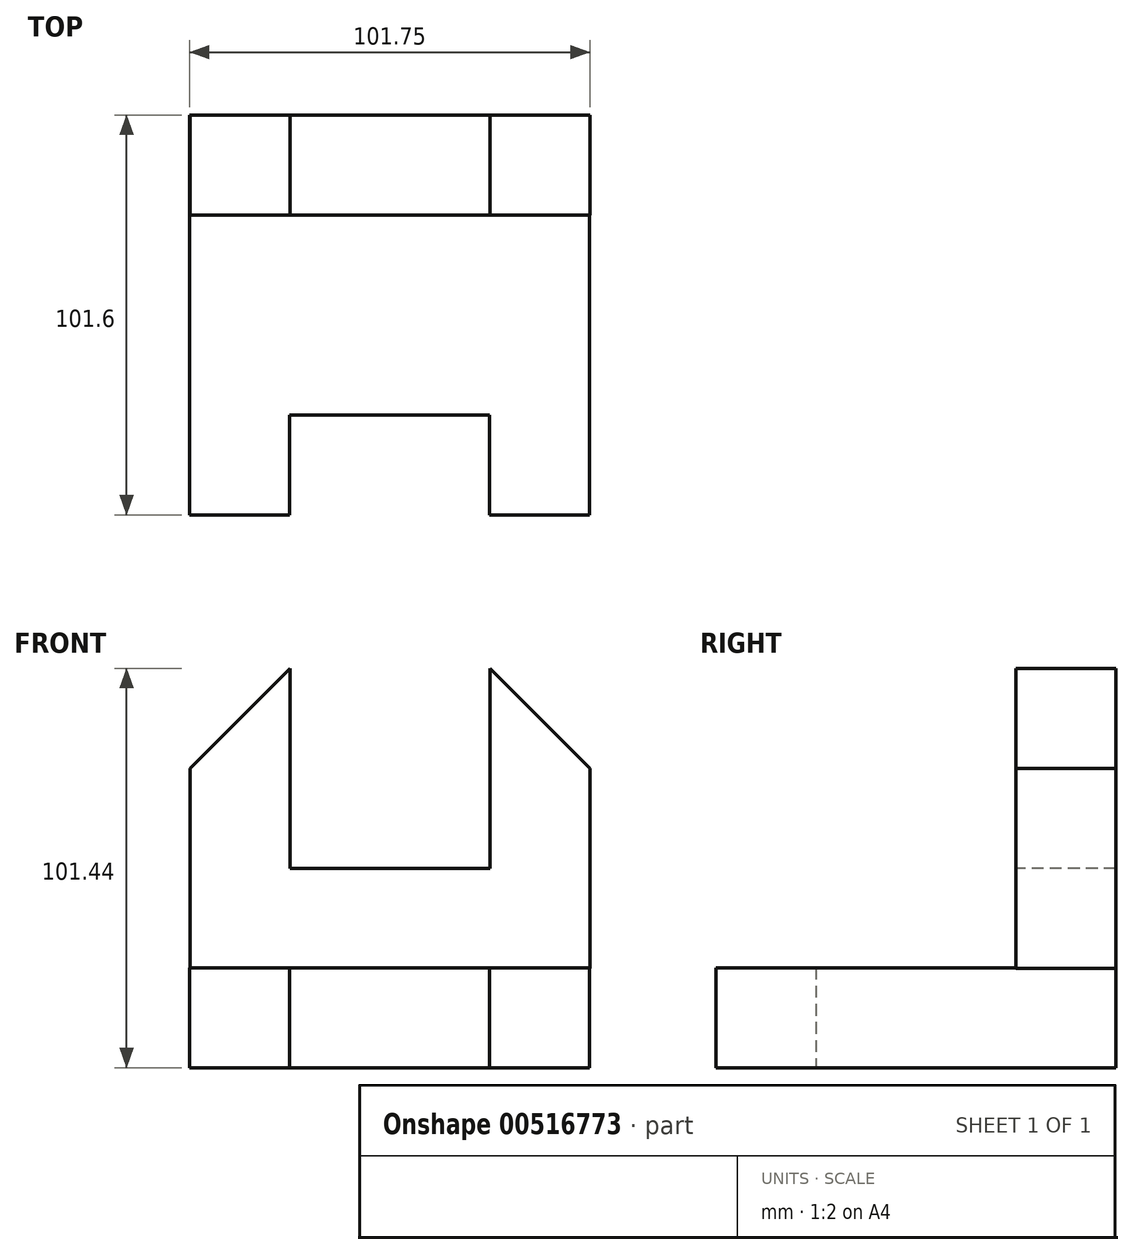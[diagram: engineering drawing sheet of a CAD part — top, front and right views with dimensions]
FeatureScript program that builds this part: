
annotation { "Feature Type Name" : "Feature", "Feature Type Description" : "" }
export const myFeature = defineFeature(function(context is Context, id is Id, definition is map)
    precondition{}
    {
        {
            var Q0;
            Q0=qCreatedBy(makeId("Top.planeOp"),FACE);
            var sketch = newSketch(context, id + "F0", { "sketchPlane" : qUnion([Q0])});
            skLineSegment(sketch, "E0", {"start": v(-50.8, 0) * mm, "end": v(-50.8, 50.8) * mm});
            skLineSegment(sketch, "E1", {"start": v(-50.8, 0) * mm, "end": v(-50.8, -50.8) * mm});
            skLineSegment(sketch, "E2", {"start": v(-50.8, -50.8) * mm, "end": v(-25.4, -50.8) * mm});
            skLineSegment(sketch, "E3", {"start": v(-25.4, -50.8) * mm, "end": v(-25.4, -25.4) * mm});
            skLineSegment(sketch, "E4", {"start": v(-25.4, -25.4) * mm, "end": v(25.4, -25.4) * mm});
            skLineSegment(sketch, "E5", {"start": v(25.4, -25.4) * mm, "end": v(25.4, -50.8) * mm});
            skLineSegment(sketch, "E6", {"start": v(25.4, -50.8) * mm, "end": v(50.8, -50.8) * mm});
            skLineSegment(sketch, "E7", {"start": v(50.8, -50.8) * mm, "end": v(50.8, 50.8) * mm});
            skLineSegment(sketch, "E8", {"start": v(50.8, 50.8) * mm, "end": v(-50.8, 50.8) * mm});
            skSolve(sketch);
        }
        {
            var Q0;
            Q0=makeQuery(id+"F0.imprint","IMPRINT",FACE,{"disambiguationData":[TD([[makeQuery(id+"F0.imprint","IMPRINT",EDGE,{"derivedFrom":sQuery(id+"F0.wireOp",EDGE,"E0")}),-1.0]])]});
            extrude(context, id + "F1", {"entities" : qUnion([Q0]), "depth" : 25.4 * mm, "offsetDistance" : 25.4 * mm});
        }
        {
            var Q0;
            Q0=qCreatedBy(makeId("Front.planeOp"),FACE);
            var sketch = newSketch(context, id + "F2", { "sketchPlane" : qUnion([Q0])});
            skLineSegment(sketch, "E9", {"start": v(-50.65, 26.25) * mm, "end": v(-50.65, 77.05) * mm});
            skLineSegment(sketch, "E10", {"start": v(-25.25, 77.05) * mm, "end": v(-25.25, 102.45) * mm});
            skLineSegment(sketch, "E11", {"start": v(-25.25, 77.05) * mm, "end": v(-25.25, 51.65) * mm});
            skLineSegment(sketch, "E12", {"start": v(-25.25, 51.65) * mm, "end": v(25.55, 51.65) * mm});
            skLineSegment(sketch, "E13", {"start": v(25.55, 51.65) * mm, "end": v(25.55, 77.05) * mm});
            skLineSegment(sketch, "E14", {"start": v(25.55, 77.05) * mm, "end": v(25.55, 102.45) * mm});
            skLineSegment(sketch, "E15", {"start": v(50.95, 26.25) * mm, "end": v(50.95, 77.05) * mm});
            skLineSegment(sketch, "E16", {"start": v(-25.25, 102.45) * mm, "end": v(-50.65, 77.05) * mm});
            skLineSegment(sketch, "E17", {"start": v(25.55, 102.45) * mm, "end": v(50.95, 77.05) * mm});
            skLineSegment(sketch, "E18", {"start": v(-50.65, 26.25) * mm, "end": v(50.95, 26.25) * mm});
            skSolve(sketch);
        }
        {
            var Q0;
            Q0=makeQuery(id+"F2.imprint","IMPRINT",FACE,{"disambiguationData":[TD([[makeQuery(id+"F2.imprint","IMPRINT",EDGE,{"derivedFrom":sQuery(id+"F2.wireOp",EDGE,"E9")}),-1.0]])]});
            extrude(context, id + "F3", {"entities" : qUnion([Q0]), "oppositeDirection" : true, "depth" : 50.8 * mm, "offsetDistance" : 25.4 * mm});
        }
        {
            var Q0;
            Q0=makeQuery(id+"F3.opExtrude","CAP_FACE",FACE,{"disambiguationData":[OSD([sQuery(id+"F2.wireOp",EDGE,"E9"),sQuery(id+"F2.wireOp",EDGE,"E10"),sQuery(id+"F2.wireOp",EDGE,"E11"),sQuery(id+"F2.wireOp",EDGE,"E12"),sQuery(id+"F2.wireOp",EDGE,"E13"),sQuery(id+"F2.wireOp",EDGE,"E14"),sQuery(id+"F2.wireOp",EDGE,"E15"),sQuery(id+"F2.wireOp",EDGE,"E16"),sQuery(id+"F2.wireOp",EDGE,"E17"),sQuery(id+"F2.wireOp",EDGE,"E18")])],"isStart":true});
            extrude(context, id + "F4", {"entities" : qUnion([Q0]), "operationType" : NewBodyOperationType.REMOVE, "oppositeDirection" : true, "depth" : 25.4 * mm, "offsetDistance" : 25.4 * mm});
        }
        {
            var Q0;
            Q0=makeQuery(id+"F3.opExtrude","SWEPT_BODY",BODY,{"disambiguationData":[OSD([sQuery(id+"F2.wireOp",EDGE,"E9"),sQuery(id+"F2.wireOp",EDGE,"E10"),sQuery(id+"F2.wireOp",EDGE,"E11"),sQuery(id+"F2.wireOp",EDGE,"E12"),sQuery(id+"F2.wireOp",EDGE,"E13"),sQuery(id+"F2.wireOp",EDGE,"E14"),sQuery(id+"F2.wireOp",EDGE,"E15"),sQuery(id+"F2.wireOp",EDGE,"E16"),sQuery(id+"F2.wireOp",EDGE,"E17"),sQuery(id+"F2.wireOp",EDGE,"E18")])]});
            transform(context, id + "F5", {"entities" : qUnion([Q0]), "transformType" : TransformType.TRANSLATION_3D, "dx" : 0 * mm, "dy" : 0 * mm, "dz" : -1.02 * mm, "makeCopy" : false});
        }
    });
